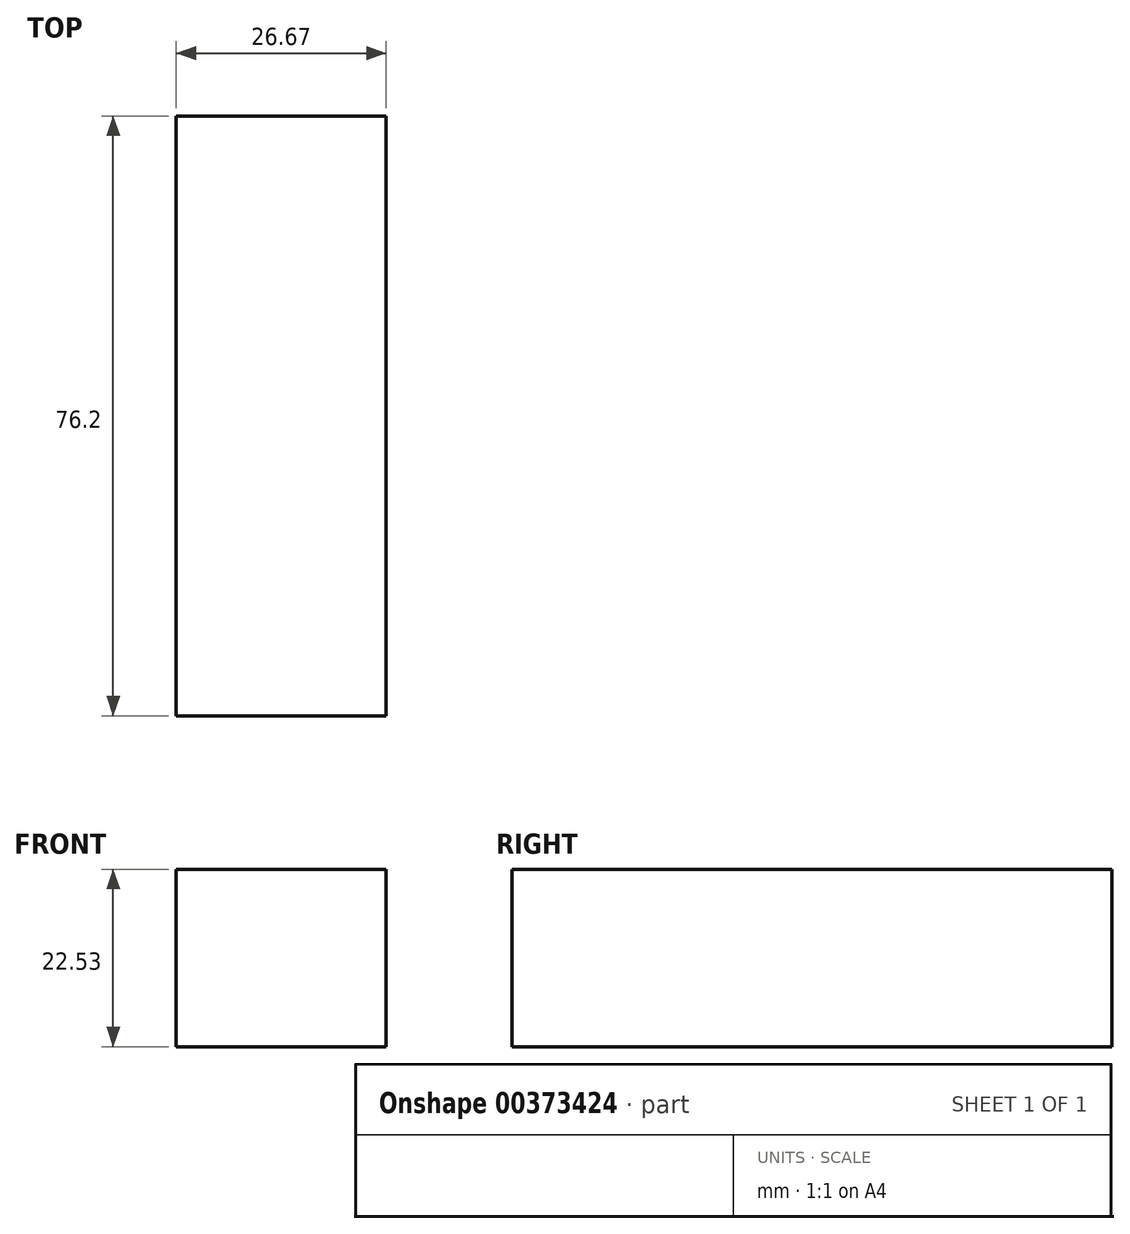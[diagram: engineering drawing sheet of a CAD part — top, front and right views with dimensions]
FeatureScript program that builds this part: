
annotation { "Feature Type Name" : "Feature", "Feature Type Description" : "" }
export const myFeature = defineFeature(function(context is Context, id is Id, definition is map)
    precondition{}
    {
        {
            var Q0;
            Q0=qCreatedBy(makeId("Front.planeOp"),FACE);
            var sketch = newSketch(context, id + "F0", { "sketchPlane" : qUnion([Q0])});
            skLineSegment(sketch, "E0.bottom", {"start": v(-63.4, 58.44) * mm, "end": v(-36.74, 58.44) * mm});
            skLineSegment(sketch, "E0.top", {"start": v(-63.4, 35.91) * mm, "end": v(-36.74, 35.91) * mm});
            skLineSegment(sketch, "E0.left", {"start": v(-63.4, 58.44) * mm, "end": v(-63.4, 35.91) * mm});
            skLineSegment(sketch, "E0.right", {"start": v(-36.74, 58.44) * mm, "end": v(-36.74, 35.91) * mm});
            skSolve(sketch);
        }
        {
            var Q0;
            Q0=makeQuery(id+"F0.imprint","IMPRINT",FACE,{"disambiguationData":[TD([[makeQuery(id+"F0.imprint","IMPRINT",EDGE,{"derivedFrom":sQuery(id+"F0.wireOp",EDGE,"E0.bottom")}),-1.0]])]});
            extrude(context, id + "F1", {"entities" : qUnion([Q0]), "depth" : 76.2 * mm});
        }
    });
